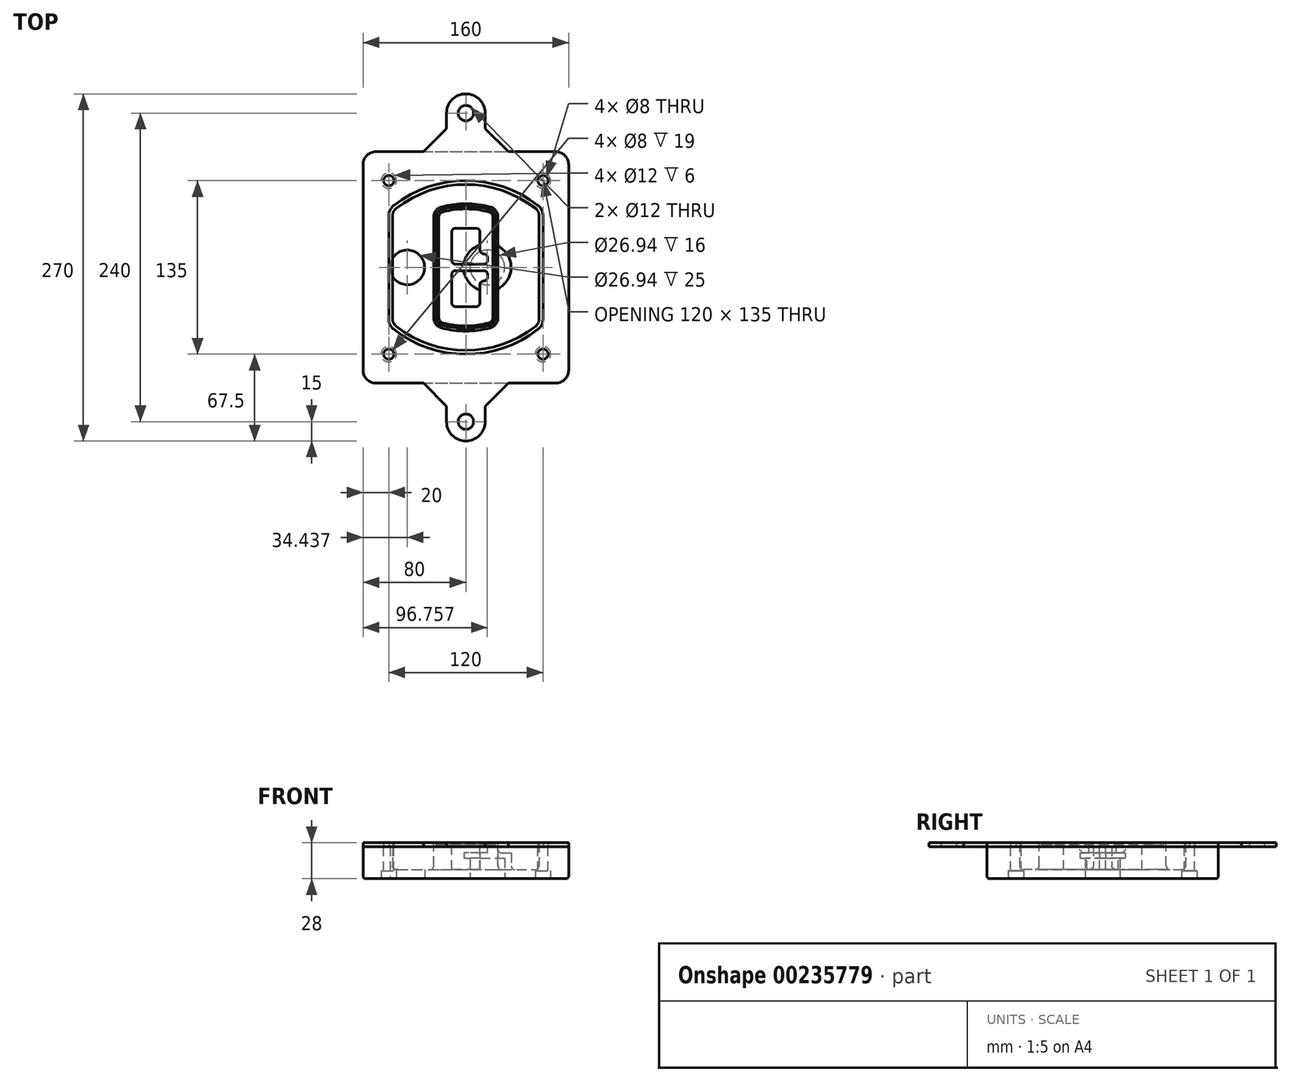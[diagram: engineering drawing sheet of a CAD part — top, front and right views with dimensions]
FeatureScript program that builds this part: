
annotation { "Feature Type Name" : "Feature", "Feature Type Description" : "" }
export const myFeature = defineFeature(function(context is Context, id is Id, definition is map)
    precondition{}
    {
        {
            var Q0;
            Q0=qCreatedBy(makeId("Top.planeOp"),FACE);
            var sketch = newSketch(context, id + "F0", { "sketchPlane" : qUnion([Q0])});
            skPoint(sketch, "E0.rect.middle", {"position": v(0, 0) * mm});
            skLineSegment(sketch, "E1.bottom", {"start": v(-70, -90) * mm, "end": v(70, -90) * mm});
            skLineSegment(sketch, "E1.top", {"start": v(-70, 90) * mm, "end": v(70, 90) * mm});
            skLineSegment(sketch, "E1.left", {"start": v(-80, -80) * mm, "end": v(-80, 80) * mm});
            skLineSegment(sketch, "E1.right", {"start": v(80, -80) * mm, "end": v(80, 80) * mm});
            skLineSegment(sketch, "E2", {"start": v(-80, 90) * mm, "end": v(80, -90) * mm, "construction": true});
            skLineSegment(sketch, "E3", {"start": v(80, 90) * mm, "end": v(-80, -90) * mm, "construction": true});
            skCircle(sketch, "E4", {"center": v(-60, 67.5) * mm, "radius": 4 * mm});
            skCircle(sketch, "E5", {"center": v(60, 67.5) * mm, "radius": 4 * mm});
            skCircle(sketch, "E6", {"center": v(60, -67.5) * mm, "radius": 4 * mm});
            skCircle(sketch, "E7", {"center": v(-60, -67.5) * mm, "radius": 4 * mm});
            skLineSegment(sketch, "E8", {"start": v(-60, 67.5) * mm, "end": v(60, 67.5) * mm, "construction": true});
            skLineSegment(sketch, "E9", {"start": v(60, 67.5) * mm, "end": v(60, -67.5) * mm, "construction": true});
            skLineSegment(sketch, "E10", {"start": v(60, -67.5) * mm, "end": v(-60, -67.5) * mm, "construction": true});
            skLineSegment(sketch, "E11", {"start": v(-60, -67.5) * mm, "end": v(-60, 67.5) * mm, "construction": true});
            skLineSegment(sketch, "E12", {"start": v(-60, 40.3) * mm, "end": v(-60, -40.3) * mm});
            skLineSegment(sketch, "E13", {"start": v(60, 40.3) * mm, "end": v(60, -40.3) * mm});
            skArc(sketch, "E14", {"start": v(56.15, 48.18) * mm, "mid": v(0, 67.5) * mm, "end": v(-56.15, 48.18) * mm});
            skArc(sketch, "E15", {"start": v(-56.15, -48.18) * mm, "mid": v(0, -67.5) * mm, "end": v(56.15, -48.18) * mm});
            skLineSegment(sketch, "E16", {"start": v(-60, 0) * mm, "end": v(60, 0) * mm, "construction": true});
            skPoint(sketch, "E17.visualSharp", {"position": v(-60, -45) * mm});
            skArc(sketch, "E17.filletArc", {"start": v(-60, -40.3) * mm, "mid": v(-58.99, -44.68) * mm, "end": v(-56.15, -48.18) * mm});
            skPoint(sketch, "E18.visualSharp", {"position": v(-60, 45) * mm});
            skArc(sketch, "E18.filletArc", {"start": v(-56.15, 48.18) * mm, "mid": v(-58.99, 44.68) * mm, "end": v(-60, 40.3) * mm});
            skPoint(sketch, "E19.visualSharp", {"position": v(60, 45) * mm});
            skArc(sketch, "E19.filletArc", {"start": v(60, 40.3) * mm, "mid": v(58.99, 44.68) * mm, "end": v(56.15, 48.18) * mm});
            skPoint(sketch, "E20.visualSharp", {"position": v(60, -45) * mm});
            skArc(sketch, "E20.filletArc", {"start": v(56.15, -48.18) * mm, "mid": v(58.99, -44.68) * mm, "end": v(60, -40.3) * mm});
            skPoint(sketch, "E21.visualSharp", {"position": v(-80, 90) * mm});
            skArc(sketch, "E21.filletArc", {"start": v(-70, 90) * mm, "mid": v(-77.07, 87.07) * mm, "end": v(-80, 80) * mm});
            skPoint(sketch, "E22.visualSharp", {"position": v(80, 90) * mm});
            skArc(sketch, "E22.filletArc", {"start": v(80, 80) * mm, "mid": v(77.07, 87.07) * mm, "end": v(70, 90) * mm});
            skPoint(sketch, "E23.visualSharp", {"position": v(80, -90) * mm});
            skArc(sketch, "E23.filletArc", {"start": v(70, -90) * mm, "mid": v(77.07, -87.07) * mm, "end": v(80, -80) * mm});
            skPoint(sketch, "E24.visualSharp", {"position": v(-80, -90) * mm});
            skArc(sketch, "E24.filletArc", {"start": v(-80, -80) * mm, "mid": v(-77.07, -87.07) * mm, "end": v(-70, -90) * mm});
            skArc(sketch, "E25.0", {"start": v(57, 40.3) * mm, "mid": v(56.3, 43.36) * mm, "end": v(54.3, 45.81) * mm});
            skLineSegment(sketch, "E25.1", {"start": v(57, 40.3) * mm, "end": v(57, -40.3) * mm});
            skArc(sketch, "E25.2", {"start": v(54.3, -45.81) * mm, "mid": v(56.3, -43.36) * mm, "end": v(57, -40.3) * mm});
            skArc(sketch, "E25.3", {"start": v(-54.3, -45.81) * mm, "mid": v(0, -64.5) * mm, "end": v(54.3, -45.81) * mm});
            skArc(sketch, "E25.4", {"start": v(-57, -40.3) * mm, "mid": v(-56.3, -43.36) * mm, "end": v(-54.3, -45.81) * mm});
            skArc(sketch, "E25.5", {"start": v(54.3, 45.81) * mm, "mid": v(0, 64.5) * mm, "end": v(-54.3, 45.81) * mm});
            skLineSegment(sketch, "E25.6", {"start": v(-57, 40.3) * mm, "end": v(-57, -40.3) * mm});
            skArc(sketch, "E25.7", {"start": v(-54.3, 45.81) * mm, "mid": v(-56.3, 43.36) * mm, "end": v(-57, 40.3) * mm});
            skArc(sketch, "E26.0", {"start": v(-58.62, 51.33) * mm, "mid": v(-62.58, 46.43) * mm, "end": v(-64, 40.3) * mm});
            skArc(sketch, "E26.1", {"start": v(58.62, 51.33) * mm, "mid": v(0, 71.5) * mm, "end": v(-58.62, 51.33) * mm});
            skArc(sketch, "E26.2", {"start": v(64, 40.3) * mm, "mid": v(62.58, 46.43) * mm, "end": v(58.62, 51.33) * mm});
            skLineSegment(sketch, "E26.3", {"start": v(64, 40.3) * mm, "end": v(64, -40.3) * mm});
            skArc(sketch, "E26.4", {"start": v(58.62, -51.33) * mm, "mid": v(62.58, -46.43) * mm, "end": v(64, -40.3) * mm});
            skLineSegment(sketch, "E26.5", {"start": v(-64, 40.3) * mm, "end": v(-64, -40.3) * mm});
            skArc(sketch, "E26.6", {"start": v(-58.62, -51.33) * mm, "mid": v(0, -71.5) * mm, "end": v(58.62, -51.33) * mm});
            skArc(sketch, "E26.7", {"start": v(-64, -40.3) * mm, "mid": v(-62.58, -46.43) * mm, "end": v(-58.62, -51.33) * mm});
            skSolve(sketch);
        }
        {
            var Q0;
            Q0=makeQuery(id+"F0.imprint","IMPRINT",FACE,{"disambiguationData":[TD([[makeQuery(id+"F0.imprint","IMPRINT",EDGE,{"derivedFrom":sQuery(id+"F0.wireOp",EDGE,"E1.bottom")}),1.0]])]});
            var Q1;
            Q1=makeQuery(id+"F0.imprint","IMPRINT",FACE,{"disambiguationData":[TD([[makeQuery(id+"F0.imprint","IMPRINT",EDGE,{"derivedFrom":sQuery(id+"F0.wireOp",EDGE,"E12")}),1.0]])]});
            var Q2;
            Q2=makeQuery(id+"F0.imprint","IMPRINT",FACE,{"disambiguationData":[TD([[makeQuery(id+"F0.imprint","IMPRINT",EDGE,{"derivedFrom":sQuery(id+"F0.wireOp",EDGE,"E25.0")}),1.0]])]});
            var Q3;
            Q3=makeQuery(id+"F0.imprint","IMPRINT",FACE,{"disambiguationData":[TD([[makeQuery(id+"F0.imprint","IMPRINT",EDGE,{"derivedFrom":sQuery(id+"F0.wireOp",EDGE,"E12")}),-1.0]])]});
            extrude(context, id + "F1", {"entities" : qUnion([Q0, Q1, Q2, Q3]), "oppositeDirection" : true, "depth" : 25 * mm});
        }
        {
            var Q0;
            Q0=makeQuery(id+"F0.imprint","IMPRINT",FACE,{"disambiguationData":[TD([[makeQuery(id+"F0.imprint","IMPRINT",EDGE,{"derivedFrom":sQuery(id+"F0.wireOp",EDGE,"E12")}),1.0]])]});
            extrude(context, id + "F2", {"entities" : qUnion([Q0]), "operationType" : NewBodyOperationType.ADD, "depth" : 3 * mm});
        }
        {
            var Q0;
            Q0=makeQuery(id+"F0.imprint","IMPRINT",FACE,{"disambiguationData":[TD([[makeQuery(id+"F0.imprint","IMPRINT",EDGE,{"derivedFrom":sQuery(id+"F0.wireOp",EDGE,"E25.0")}),1.0]])]});
            extrude(context, id + "F3", {"entities" : qUnion([Q0]), "operationType" : NewBodyOperationType.REMOVE, "oppositeDirection" : true, "depth" : 18 * mm});
        }
        {
            var Q0;
            Q0=makeQuery(id+"F2.opExtrude","CAP_FACE",FACE,{"disambiguationData":[OSD([sQuery(id+"F0.wireOp",EDGE,"E12"),sQuery(id+"F0.wireOp",EDGE,"E13"),sQuery(id+"F0.wireOp",EDGE,"E14"),sQuery(id+"F0.wireOp",EDGE,"E15"),sQuery(id+"F0.wireOp",EDGE,"E17.filletArc"),sQuery(id+"F0.wireOp",EDGE,"E18.filletArc"),sQuery(id+"F0.wireOp",EDGE,"E19.filletArc"),sQuery(id+"F0.wireOp",EDGE,"E20.filletArc"),sQuery(id+"F0.wireOp",EDGE,"E25.0"),sQuery(id+"F0.wireOp",EDGE,"E25.1"),sQuery(id+"F0.wireOp",EDGE,"E25.2"),sQuery(id+"F0.wireOp",EDGE,"E25.3"),sQuery(id+"F0.wireOp",EDGE,"E25.4"),sQuery(id+"F0.wireOp",EDGE,"E25.5"),sQuery(id+"F0.wireOp",EDGE,"E25.6"),sQuery(id+"F0.wireOp",EDGE,"E25.7")])],"isStart":false});
            var sketch = newSketch(context, id + "F4", { "sketchPlane" : qUnion([Q0])});
            skArc(sketch, "E27.0", {"start": v(-19.08, -46.97) * mm, "mid": v(0, -49.5) * mm, "end": v(19.08, -46.97) * mm});
            skArc(sketch, "E28.0", {"start": v(19.08, 46.97) * mm, "mid": v(0, 49.5) * mm, "end": v(-19.08, 46.97) * mm});
            skLineSegment(sketch, "E29", {"start": v(-25, 39.25) * mm, "end": v(-25, -39.25) * mm});
            skLineSegment(sketch, "E30", {"start": v(25, 39.25) * mm, "end": v(25, -39.25) * mm});
            skLineSegment(sketch, "E31", {"start": v(-25, 45.1) * mm, "end": v(25, 45.1) * mm, "construction": true});
            skLineSegment(sketch, "E32", {"start": v(-25, -45.1) * mm, "end": v(25, -45.1) * mm, "construction": true});
            skPoint(sketch, "E33.visualSharp", {"position": v(-25, 45.1) * mm});
            skArc(sketch, "E33.filletArc", {"start": v(-19.08, 46.97) * mm, "mid": v(-23.35, 44.11) * mm, "end": v(-25, 39.25) * mm});
            skPoint(sketch, "E34.visualSharp", {"position": v(25, 45.1) * mm});
            skArc(sketch, "E34.filletArc", {"start": v(25, 39.25) * mm, "mid": v(23.35, 44.11) * mm, "end": v(19.08, 46.97) * mm});
            skPoint(sketch, "E35.visualSharp", {"position": v(25, -45.1) * mm});
            skArc(sketch, "E35.filletArc", {"start": v(19.08, -46.97) * mm, "mid": v(23.35, -44.11) * mm, "end": v(25, -39.25) * mm});
            skPoint(sketch, "E36.visualSharp", {"position": v(-25, -45.1) * mm});
            skArc(sketch, "E36.filletArc", {"start": v(-25, -39.25) * mm, "mid": v(-23.35, -44.11) * mm, "end": v(-19.08, -46.97) * mm});
            skArc(sketch, "E37.0", {"start": v(54.3, 45.81) * mm, "mid": v(0, 64.5) * mm, "end": v(-54.3, 45.81) * mm});
            skArc(sketch, "E37.1", {"start": v(-54.3, 45.81) * mm, "mid": v(-56.3, 43.36) * mm, "end": v(-57, 40.3) * mm});
            skLineSegment(sketch, "E37.2", {"start": v(-57, 40.3) * mm, "end": v(-57, -40.3) * mm});
            skArc(sketch, "E37.3", {"start": v(-57, -40.3) * mm, "mid": v(-56.3, -43.36) * mm, "end": v(-54.3, -45.81) * mm});
            skArc(sketch, "E37.4", {"start": v(-54.3, -45.81) * mm, "mid": v(0, -64.5) * mm, "end": v(54.3, -45.81) * mm});
            skArc(sketch, "E37.5", {"start": v(54.3, -45.81) * mm, "mid": v(56.3, -43.36) * mm, "end": v(57, -40.3) * mm});
            skLineSegment(sketch, "E37.6", {"start": v(57, 40.3) * mm, "end": v(57, -40.3) * mm});
            skArc(sketch, "E37.7", {"start": v(57, 40.3) * mm, "mid": v(56.3, 43.36) * mm, "end": v(54.3, 45.81) * mm});
            skLineSegment(sketch, "E38.0", {"start": v(23, 39.25) * mm, "end": v(23, -39.25) * mm});
            skArc(sketch, "E38.1", {"start": v(18.56, -45.04) * mm, "mid": v(21.76, -42.9) * mm, "end": v(23, -39.25) * mm});
            skArc(sketch, "E38.2", {"start": v(-18.56, -45.04) * mm, "mid": v(0, -47.5) * mm, "end": v(18.56, -45.04) * mm});
            skArc(sketch, "E38.3", {"start": v(-23, -39.25) * mm, "mid": v(-21.76, -42.9) * mm, "end": v(-18.56, -45.04) * mm});
            skLineSegment(sketch, "E38.4", {"start": v(-23, 39.25) * mm, "end": v(-23, -39.25) * mm});
            skArc(sketch, "E38.5", {"start": v(23, 39.25) * mm, "mid": v(21.76, 42.9) * mm, "end": v(18.56, 45.04) * mm});
            skArc(sketch, "E38.6", {"start": v(-18.56, 45.04) * mm, "mid": v(-21.76, 42.9) * mm, "end": v(-23, 39.25) * mm});
            skArc(sketch, "E38.7", {"start": v(18.56, 45.04) * mm, "mid": v(0, 47.5) * mm, "end": v(-18.56, 45.04) * mm});
            skArc(sketch, "E39.0", {"start": v(21, 39.25) * mm, "mid": v(20.18, 41.68) * mm, "end": v(18.04, 43.1) * mm});
            skLineSegment(sketch, "E39.1", {"start": v(21, 39.25) * mm, "end": v(21, -39.25) * mm});
            skArc(sketch, "E39.2", {"start": v(18.04, -43.1) * mm, "mid": v(20.18, -41.68) * mm, "end": v(21, -39.25) * mm});
            skArc(sketch, "E39.3", {"start": v(-18.04, -43.1) * mm, "mid": v(0, -45.5) * mm, "end": v(18.04, -43.1) * mm});
            skArc(sketch, "E39.4", {"start": v(-21, -39.25) * mm, "mid": v(-20.18, -41.68) * mm, "end": v(-18.04, -43.1) * mm});
            skArc(sketch, "E39.5", {"start": v(18.04, 43.1) * mm, "mid": v(0, 45.5) * mm, "end": v(-18.04, 43.1) * mm});
            skLineSegment(sketch, "E39.6", {"start": v(-21, 39.25) * mm, "end": v(-21, -39.25) * mm});
            skArc(sketch, "E39.7", {"start": v(-18.04, 43.1) * mm, "mid": v(-20.18, 41.68) * mm, "end": v(-21, 39.25) * mm});
            skLineSegment(sketch, "E40", {"start": v(-25, 0) * mm, "end": v(25, 0) * mm, "construction": true});
            skLineSegment(sketch, "E41", {"start": v(-11, 5.5) * mm, "end": v(-11, 27.5) * mm});
            skLineSegment(sketch, "E42", {"start": v(-8, 30.5) * mm, "end": v(8, 30.5) * mm});
            skLineSegment(sketch, "E43", {"start": v(11, 27.5) * mm, "end": v(11, 13.5) * mm});
            skLineSegment(sketch, "E44", {"start": v(14, 10.5) * mm, "end": v(14, 10.5) * mm});
            skLineSegment(sketch, "E45", {"start": v(17, 7.5) * mm, "end": v(17, 5.5) * mm});
            skLineSegment(sketch, "E46", {"start": v(14, 2.5) * mm, "end": v(-8, 2.5) * mm});
            skPoint(sketch, "E47.visualSharp", {"position": v(-11, 30.5) * mm});
            skArc(sketch, "E47.filletArc", {"start": v(-8, 30.5) * mm, "mid": v(-10.12, 29.62) * mm, "end": v(-11, 27.5) * mm});
            skPoint(sketch, "E48.visualSharp", {"position": v(11, 30.5) * mm});
            skArc(sketch, "E48.filletArc", {"start": v(11, 27.5) * mm, "mid": v(10.12, 29.62) * mm, "end": v(8, 30.5) * mm});
            skPoint(sketch, "E49.visualSharp", {"position": v(11, 10.5) * mm});
            skArc(sketch, "E49.filletArc", {"start": v(11, 13.5) * mm, "mid": v(11.88, 11.38) * mm, "end": v(14, 10.5) * mm});
            skPoint(sketch, "E50.visualSharp", {"position": v(17, 10.5) * mm});
            skArc(sketch, "E50.filletArc", {"start": v(17, 7.5) * mm, "mid": v(16.12, 9.62) * mm, "end": v(14, 10.5) * mm});
            skPoint(sketch, "E51.visualSharp", {"position": v(17, 2.5) * mm});
            skArc(sketch, "E51.filletArc", {"start": v(14, 2.5) * mm, "mid": v(16.12, 3.38) * mm, "end": v(17, 5.5) * mm});
            skPoint(sketch, "E52.visualSharp", {"position": v(-11, 2.5) * mm});
            skArc(sketch, "E52.filletArc", {"start": v(-11, 5.5) * mm, "mid": v(-10.12, 3.38) * mm, "end": v(-8, 2.5) * mm});
            skLineSegment(sketch, "E53.0.MirrorCS", {"start": v(14, -2.5) * mm, "end": v(-8, -2.5) * mm});
            skArc(sketch, "E54.0.MirrorCS", {"start": v(-11, -5.5) * mm, "mid": v(-10.12, -3.38) * mm, "end": v(-8, -2.5) * mm});
            skLineSegment(sketch, "E55.0.MirrorCS", {"start": v(-11, -5.5) * mm, "end": v(-11, -27.5) * mm});
            skArc(sketch, "E56.0.MirrorCS", {"start": v(-8, -30.5) * mm, "mid": v(-10.12, -29.62) * mm, "end": v(-11, -27.5) * mm});
            skLineSegment(sketch, "E57.0.MirrorCS", {"start": v(-8, -30.5) * mm, "end": v(8, -30.5) * mm});
            skArc(sketch, "E58.0.MirrorCS", {"start": v(11, -27.5) * mm, "mid": v(10.12, -29.62) * mm, "end": v(8, -30.5) * mm});
            skLineSegment(sketch, "E59.0.MirrorCS", {"start": v(11, -27.5) * mm, "end": v(11, -13.5) * mm});
            skArc(sketch, "E60.0.MirrorCS", {"start": v(11, -13.5) * mm, "mid": v(11.88, -11.38) * mm, "end": v(14, -10.5) * mm});
            skArc(sketch, "E61.0.MirrorCS", {"start": v(17, -7.5) * mm, "mid": v(16.12, -9.62) * mm, "end": v(14, -10.5) * mm});
            skLineSegment(sketch, "E62.0.MirrorCS", {"start": v(17, -7.5) * mm, "end": v(17, -5.5) * mm});
            skArc(sketch, "E63.0.MirrorCS", {"start": v(14, -2.5) * mm, "mid": v(16.12, -3.38) * mm, "end": v(17, -5.5) * mm});
            skSolve(sketch);
        }
        {
            var Q0;
            Q0=makeQuery(id+"F4.imprint","IMPRINT",FACE,{"disambiguationData":[TD([[makeQuery(id+"F4.imprint","IMPRINT",EDGE,{"derivedFrom":sQuery(id+"F4.wireOp",EDGE,"E27.0")}),1.0]])]});
            var Q1;
            Q1=makeQuery(id+"F4.imprint","IMPRINT",FACE,{"disambiguationData":[TD([[makeQuery(id+"F4.imprint","IMPRINT",EDGE,{"derivedFrom":sQuery(id+"F4.wireOp",EDGE,"E38.0")}),-1.0]])]});
            var Q2;
            Q2=makeQuery(id+"F4.imprint","IMPRINT",FACE,{"disambiguationData":[TD([[makeQuery(id+"F4.imprint","IMPRINT",EDGE,{"derivedFrom":sQuery(id+"F4.wireOp",EDGE,"E39.0")}),1.0]])]});
            extrude(context, id + "F5", {"entities" : qUnion([Q0, Q1, Q2]), "operationType" : NewBodyOperationType.ADD, "endBound" : BoundingType.UP_TO_NEXT, "oppositeDirection" : true, "depth" : 25 * mm});
        }
        {
            var Q0;
            Q0=makeQuery(id+"F4.imprint","IMPRINT",FACE,{"disambiguationData":[TD([[makeQuery(id+"F4.imprint","IMPRINT",EDGE,{"derivedFrom":sQuery(id+"F4.wireOp",EDGE,"E38.0")}),-1.0]])]});
            extrude(context, id + "F6", {"entities" : qUnion([Q0]), "operationType" : NewBodyOperationType.REMOVE, "oppositeDirection" : true, "depth" : 2 * mm});
        }
        {
            var Q0;
            Q0=makeQuery(id+"F1.opExtrude","CAP_FACE",FACE,{"disambiguationData":[OSD([sQuery(id+"F0.wireOp",EDGE,"E1.bottom"),sQuery(id+"F0.wireOp",EDGE,"E1.top"),sQuery(id+"F0.wireOp",EDGE,"E1.left"),sQuery(id+"F0.wireOp",EDGE,"E1.right"),sQuery(id+"F0.wireOp",EDGE,"E4"),sQuery(id+"F0.wireOp",EDGE,"E5"),sQuery(id+"F0.wireOp",EDGE,"E6"),sQuery(id+"F0.wireOp",EDGE,"E7"),sQuery(id+"F0.wireOp",EDGE,"E21.filletArc"),sQuery(id+"F0.wireOp",EDGE,"E22.filletArc"),sQuery(id+"F0.wireOp",EDGE,"E23.filletArc"),sQuery(id+"F0.wireOp",EDGE,"E24.filletArc")])],"isStart":false});
            var sketch = newSketch(context, id + "F7", { "sketchPlane" : qUnion([Q0])});
            skCircle(sketch, "E64", {"center": v(16.76, 0) * mm, "radius": 13.47 * mm});
            skCircle(sketch, "E65", {"center": v(-45.56, 0) * mm, "radius": 13.47 * mm});
            skLineSegment(sketch, "E66", {"start": v(80, 0) * mm, "end": v(-80, 0) * mm});
            skCircle(sketch, "E67", {"center": v(16.76, 0) * mm, "radius": 18.47 * mm});
            skCircle(sketch, "E68", {"center": v(60, -67.5) * mm, "radius": 6 * mm});
            skCircle(sketch, "E69", {"center": v(-60, -67.5) * mm, "radius": 6 * mm});
            skCircle(sketch, "E70", {"center": v(-60, 67.5) * mm, "radius": 6 * mm});
            skCircle(sketch, "E71", {"center": v(60, 67.5) * mm, "radius": 6 * mm});
            skSolve(sketch);
        }
        {
            var Q0;
            {var subQ1=sQuery(id+"F7.wireOp",EDGE,"E66");var subQ4=sQuery(id+"F7.wireOp",EDGE,"E64");var subQ6=makeQuery(id+"F7.imprint","INTERSECT",VERTEX,{"disambiguationData":[OD(0.0)],"derivedFrom":[subQ4,subQ1]});Q0=makeQuery(id+"F7.imprint","IMPRINT",FACE,{"disambiguationData":[TD([[makeQuery(id+"F7.imprint","IMPRINT",EDGE,{"disambiguationData":[TD([[subQ6,-1.0]])],"derivedFrom":subQ4}),-1.0]])]});}
            var Q1;
            {var subQ0=sQuery(id+"F7.wireOp",EDGE,"E66");var subQ1=sQuery(id+"F7.wireOp",EDGE,"E64");var subQ3=makeQuery(id+"F7.imprint","INTERSECT",VERTEX,{"disambiguationData":[OD(0.0)],"derivedFrom":[subQ1,subQ0]});Q1=makeQuery(id+"F7.imprint","IMPRINT",FACE,{"disambiguationData":[TD([[makeQuery(id+"F7.imprint","IMPRINT",EDGE,{"disambiguationData":[TD([[subQ3,-1.0]])],"derivedFrom":subQ1}),1.0]])]});}
            var Q2;
            {var subQ0=sQuery(id+"F7.wireOp",EDGE,"E66");var subQ1=sQuery(id+"F7.wireOp",EDGE,"E64");var subQ3=makeQuery(id+"F7.imprint","INTERSECT",VERTEX,{"disambiguationData":[OD(0.0)],"derivedFrom":[subQ1,subQ0]});Q2=makeQuery(id+"F7.imprint","IMPRINT",FACE,{"disambiguationData":[TD([[makeQuery(id+"F7.imprint","IMPRINT",EDGE,{"disambiguationData":[TD([[subQ3,1.0]])],"derivedFrom":subQ1}),1.0]])]});}
            var Q3;
            {var subQ1=sQuery(id+"F7.wireOp",EDGE,"E66");var subQ4=sQuery(id+"F7.wireOp",EDGE,"E64");var subQ6=makeQuery(id+"F7.imprint","INTERSECT",VERTEX,{"disambiguationData":[OD(0.0)],"derivedFrom":[subQ4,subQ1]});Q3=makeQuery(id+"F7.imprint","IMPRINT",FACE,{"disambiguationData":[TD([[makeQuery(id+"F7.imprint","IMPRINT",EDGE,{"disambiguationData":[TD([[subQ6,1.0]])],"derivedFrom":subQ4}),-1.0]])]});}
            extrude(context, id + "F8", {"entities" : qUnion([Q0, Q1, Q2, Q3]), "operationType" : NewBodyOperationType.ADD, "oppositeDirection" : true, "depth" : 20 * mm});
        }
        {
            var Q0;
            {var subQ0=sQuery(id+"F7.wireOp",EDGE,"E66");var subQ1=sQuery(id+"F7.wireOp",EDGE,"E64");var subQ3=makeQuery(id+"F7.imprint","INTERSECT",VERTEX,{"disambiguationData":[OD(0.0)],"derivedFrom":[subQ1,subQ0]});Q0=makeQuery(id+"F7.imprint","IMPRINT",FACE,{"disambiguationData":[TD([[makeQuery(id+"F7.imprint","IMPRINT",EDGE,{"disambiguationData":[TD([[subQ3,-1.0]])],"derivedFrom":subQ1}),1.0]])]});}
            var Q1;
            {var subQ0=sQuery(id+"F7.wireOp",EDGE,"E66");var subQ1=sQuery(id+"F7.wireOp",EDGE,"E64");var subQ3=makeQuery(id+"F7.imprint","INTERSECT",VERTEX,{"disambiguationData":[OD(0.0)],"derivedFrom":[subQ1,subQ0]});Q1=makeQuery(id+"F7.imprint","IMPRINT",FACE,{"disambiguationData":[TD([[makeQuery(id+"F7.imprint","IMPRINT",EDGE,{"disambiguationData":[TD([[subQ3,1.0]])],"derivedFrom":subQ1}),1.0]])]});}
            extrude(context, id + "F9", {"entities" : qUnion([Q0, Q1]), "operationType" : NewBodyOperationType.REMOVE, "oppositeDirection" : true, "depth" : 16 * mm});
        }
        {
            var Q0;
            {var subQ0=sQuery(id+"F7.wireOp",EDGE,"E66");var subQ1=sQuery(id+"F7.wireOp",EDGE,"E65");var subQ3=makeQuery(id+"F7.imprint","INTERSECT",VERTEX,{"disambiguationData":[OD(0.0)],"derivedFrom":[subQ1,subQ0]});Q0=makeQuery(id+"F7.imprint","IMPRINT",FACE,{"disambiguationData":[TD([[makeQuery(id+"F7.imprint","IMPRINT",EDGE,{"disambiguationData":[TD([[subQ3,-1.0]])],"derivedFrom":subQ1}),1.0]])]});}
            var Q1;
            {var subQ0=sQuery(id+"F7.wireOp",EDGE,"E66");var subQ1=sQuery(id+"F7.wireOp",EDGE,"E65");var subQ3=makeQuery(id+"F7.imprint","INTERSECT",VERTEX,{"disambiguationData":[OD(0.0)],"derivedFrom":[subQ1,subQ0]});Q1=makeQuery(id+"F7.imprint","IMPRINT",FACE,{"disambiguationData":[TD([[makeQuery(id+"F7.imprint","IMPRINT",EDGE,{"disambiguationData":[TD([[subQ3,1.0]])],"derivedFrom":subQ1}),1.0]])]});}
            extrude(context, id + "F10", {"entities" : qUnion([Q0, Q1]), "operationType" : NewBodyOperationType.REMOVE, "oppositeDirection" : true, "depth" : 25 * mm});
        }
        {
            var Q0;
            Q0=makeQuery(id+"F7.imprint","IMPRINT",FACE,{"disambiguationData":[TD([[makeQuery(id+"F7.imprint","IMPRINT",EDGE,{"derivedFrom":sQuery(id+"F7.wireOp",EDGE,"E68")}),1.0]])]});
            var Q1;
            Q1=makeQuery(id+"F7.imprint","IMPRINT",FACE,{"disambiguationData":[TD([[makeQuery(id+"F7.imprint","IMPRINT",EDGE,{"derivedFrom":makeQuery(id+"F1.opExtrude","CAP_EDGE",EDGE,{"disambiguationData":[OSD([sQuery(id+"F0.wireOp",EDGE,"E5")])],"isStart":false})}),-1.0]])]});
            var Q2;
            Q2=makeQuery(id+"F7.imprint","IMPRINT",FACE,{"disambiguationData":[TD([[makeQuery(id+"F7.imprint","IMPRINT",EDGE,{"derivedFrom":sQuery(id+"F7.wireOp",EDGE,"E69")}),1.0]])]});
            var Q3;
            Q3=makeQuery(id+"F7.imprint","IMPRINT",FACE,{"disambiguationData":[TD([[makeQuery(id+"F7.imprint","IMPRINT",EDGE,{"derivedFrom":makeQuery(id+"F1.opExtrude","CAP_EDGE",EDGE,{"disambiguationData":[OSD([sQuery(id+"F0.wireOp",EDGE,"E4")])],"isStart":false})}),-1.0]])]});
            var Q4;
            Q4=makeQuery(id+"F7.imprint","IMPRINT",FACE,{"disambiguationData":[TD([[makeQuery(id+"F7.imprint","IMPRINT",EDGE,{"derivedFrom":sQuery(id+"F7.wireOp",EDGE,"E70")}),1.0]])]});
            var Q5;
            Q5=makeQuery(id+"F7.imprint","IMPRINT",FACE,{"disambiguationData":[TD([[makeQuery(id+"F7.imprint","IMPRINT",EDGE,{"derivedFrom":makeQuery(id+"F1.opExtrude","CAP_EDGE",EDGE,{"disambiguationData":[OSD([sQuery(id+"F0.wireOp",EDGE,"E7")])],"isStart":false})}),-1.0]])]});
            var Q6;
            Q6=makeQuery(id+"F7.imprint","IMPRINT",FACE,{"disambiguationData":[TD([[makeQuery(id+"F7.imprint","IMPRINT",EDGE,{"derivedFrom":sQuery(id+"F7.wireOp",EDGE,"E71")}),1.0]])]});
            var Q7;
            Q7=makeQuery(id+"F7.imprint","IMPRINT",FACE,{"disambiguationData":[TD([[makeQuery(id+"F7.imprint","IMPRINT",EDGE,{"derivedFrom":makeQuery(id+"F1.opExtrude","CAP_EDGE",EDGE,{"disambiguationData":[OSD([sQuery(id+"F0.wireOp",EDGE,"E6")])],"isStart":false})}),-1.0]])]});
            extrude(context, id + "F11", {"entities" : qUnion([Q0, Q1, Q2, Q3, Q4, Q5, Q6, Q7]), "operationType" : NewBodyOperationType.REMOVE, "oppositeDirection" : true, "depth" : 6 * mm});
        }
        {
            var Q0;
            Q0=makeQuery(id+"F9.boolean.opBoolean","COPY",FACE,{"derivedFrom":makeQuery(id+"F9.opExtrude","CAP_FACE",FACE,{"disambiguationData":[OSD([sQuery(id+"F7.wireOp",EDGE,"E64")])],"isStart":false})});
            var sketch = newSketch(context, id + "F12", { "sketchPlane" : qUnion([Q0])});
            skArc(sketch, "E72.0", {"start": v(11, 17.55) * mm, "mid": v(2.57, 11.82) * mm, "end": v(-1.54, 2.5) * mm});
            skArc(sketch, "E72.1", {"start": v(-1.54, -2.5) * mm, "mid": v(2.57, -11.82) * mm, "end": v(11, -17.55) * mm});
            skLineSegment(sketch, "E73", {"start": v(-1.54, -2.5) * mm, "end": v(14, -2.5) * mm});
            skLineSegment(sketch, "E74.0", {"start": v(14, 2.5) * mm, "end": v(-1.54, 2.5) * mm});
            skArc(sketch, "E74.1", {"start": v(14, 2.5) * mm, "mid": v(16.12, 3.38) * mm, "end": v(17, 5.5) * mm});
            skLineSegment(sketch, "E74.2", {"start": v(17, 7.5) * mm, "end": v(17, 5.5) * mm});
            skArc(sketch, "E74.3", {"start": v(17, 7.5) * mm, "mid": v(16.12, 9.62) * mm, "end": v(14, 10.5) * mm});
            skArc(sketch, "E74.4", {"start": v(11, 13.5) * mm, "mid": v(11.88, 11.38) * mm, "end": v(14, 10.5) * mm});
            skLineSegment(sketch, "E74.5", {"start": v(11, 17.55) * mm, "end": v(11, 13.5) * mm});
            skLineSegment(sketch, "E74.7", {"start": v(14, -2.5) * mm, "end": v(-1.54, -2.5) * mm});
            skArc(sketch, "E74.8", {"start": v(14, -2.5) * mm, "mid": v(16.12, -3.38) * mm, "end": v(17, -5.5) * mm});
            skLineSegment(sketch, "E74.9", {"start": v(17, -7.5) * mm, "end": v(17, -5.5) * mm});
            skArc(sketch, "E74.10", {"start": v(17, -7.5) * mm, "mid": v(16.12, -9.62) * mm, "end": v(14, -10.5) * mm});
            skArc(sketch, "E74.11", {"start": v(11, -13.5) * mm, "mid": v(11.88, -11.38) * mm, "end": v(14, -10.5) * mm});
            skLineSegment(sketch, "E74.12", {"start": v(11, -17.55) * mm, "end": v(11, -13.5) * mm});
            skPoint(sketch, "E75.orphan", {"position": v(11, -27.5) * mm});
            skPoint(sketch, "E76.orphan", {"position": v(-8, -2.5) * mm});
            skPoint(sketch, "E77.orphan", {"position": v(-8, 2.5) * mm});
            skPoint(sketch, "E78.orphan", {"position": v(11, 27.5) * mm});
            skSolve(sketch);
        }
        {
            var Q0;
            {var subQ7=sQuery(id+"F12.wireOp",EDGE,"E72.0");var subQ14=sQuery(id+"F12.wireOp",EDGE,"E72.1");var subQ16=sQuery(id+"F12.wireOp",EDGE,"E74.1");var subQ18=sQuery(id+"F12.wireOp",EDGE,"E74.8");Q0=qUnion([makeQuery(id+"F12.imprint","IMPRINT",FACE,{"disambiguationData":[TD([[makeQuery(id+"F12.imprint","IMPRINT",EDGE,{"derivedFrom":subQ7}),1.0]])]}),makeQuery(id+"F12.imprint","IMPRINT",FACE,{"disambiguationData":[TD([[makeQuery(id+"F12.imprint","IMPRINT",EDGE,{"derivedFrom":subQ14}),1.0]])]}),makeQuery(id+"F12.imprint","IMPRINT",FACE,{"disambiguationData":[TD([[makeQuery(id+"F12.imprint","IMPRINT",EDGE,{"derivedFrom":subQ16}),1.0]])]}),makeQuery(id+"F12.imprint","IMPRINT",FACE,{"disambiguationData":[TD([[makeQuery(id+"F12.imprint","IMPRINT",EDGE,{"derivedFrom":subQ18}),-1.0]])]})]);}
            var Q1;
            Q1=makeQuery(id+"F5.boolean.opBoolean","SPLIT",FACE,{"disambiguationData":[TD([makeQuery(id+"F5.opExtrude","SWEPT_FACE",FACE,{"disambiguationData":[OSD([sQuery(id+"F4.wireOp",EDGE,"E41")])]})])],"derivedFrom":makeQuery(id+"F3.boolean.opBoolean","COPY",FACE,{"derivedFrom":makeQuery(id+"F3.opExtrude","CAP_FACE",FACE,{"disambiguationData":[OSD([sQuery(id+"F0.wireOp",EDGE,"E25.0"),sQuery(id+"F0.wireOp",EDGE,"E25.1"),sQuery(id+"F0.wireOp",EDGE,"E25.2"),sQuery(id+"F0.wireOp",EDGE,"E25.3"),sQuery(id+"F0.wireOp",EDGE,"E25.4"),sQuery(id+"F0.wireOp",EDGE,"E25.5"),sQuery(id+"F0.wireOp",EDGE,"E25.6"),sQuery(id+"F0.wireOp",EDGE,"E25.7")])],"isStart":false})})});
            extrude(context, id + "F13", {"entities" : qUnion([Q0]), "operationType" : NewBodyOperationType.REMOVE, "endBound" : BoundingType.UP_TO_SURFACE, "endBoundEntityFace" : qUnion([Q1]), "depth" : 25 * mm});
        }
        {
            var Q0;
            Q0=makeQuery(id+"F3.boolean.opBoolean","COPY",EDGE,{"derivedFrom":makeQuery(id+"F3.opExtrude","CAP_EDGE",EDGE,{"disambiguationData":[OSD([sQuery(id+"F0.wireOp",EDGE,"E25.6")])],"isStart":false})});
            var Q1;
            Q1=makeQuery(id+"F8.boolean.opBoolean","INTERSECT",EDGE,{"derivedFrom":[makeQuery(id+"F5.opExtrude","SWEPT_FACE",FACE,{"disambiguationData":[OSD([sQuery(id+"F4.wireOp",EDGE,"E30")])]}),makeQuery(id+"F8.opExtrude","CAP_FACE",FACE,{"disambiguationData":[OSD([sQuery(id+"F7.wireOp",EDGE,"E67")])],"isStart":false})]});
            var Q2;
            Q2=makeQuery(id+"F8.boolean.opBoolean","INTERSECT",EDGE,{"disambiguationData":[OD(1.0)],"derivedFrom":[makeQuery(id+"F5.opExtrude","SWEPT_FACE",FACE,{"disambiguationData":[OSD([sQuery(id+"F4.wireOp",EDGE,"E30")])]}),makeQuery(id+"F8.opExtrude","SWEPT_FACE",FACE,{"disambiguationData":[OSD([sQuery(id+"F7.wireOp",EDGE,"E67")])]})]});
            var Q3;
            {var subQ0=sQuery(id+"F4.wireOp",EDGE,"E30");Q3=makeQuery(id+"F8.boolean.opBoolean","SPLIT",EDGE,{"disambiguationData":[TD([makeQuery(id+"F5.opExtrude","SWEPT_FACE",FACE,{"disambiguationData":[OSD([sQuery(id+"F4.wireOp",EDGE,"E35.filletArc")])]})])],"derivedFrom":makeQuery(id+"F5.opExtrude","CAP_EDGE",EDGE,{"disambiguationData":[OSD([subQ0])],"isStart":false})});}
            var Q4;
            {var subQ0=sQuery(id+"F0.wireOp",EDGE,"E25.7");var subQ1=sQuery(id+"F0.wireOp",EDGE,"E25.1");var subQ2=sQuery(id+"F0.wireOp",EDGE,"E25.6");var subQ3=sQuery(id+"F0.wireOp",EDGE,"E25.5");var subQ4=sQuery(id+"F0.wireOp",EDGE,"E25.4");var subQ5=sQuery(id+"F0.wireOp",EDGE,"E25.0");var subQ6=sQuery(id+"F0.wireOp",EDGE,"E25.2");var subQ7=sQuery(id+"F0.wireOp",EDGE,"E25.3");Q4=makeQuery(id+"F8.boolean.opBoolean","INTERSECT",EDGE,{"derivedFrom":[makeQuery(id+"F5.boolean.opBoolean","SPLIT",FACE,{"disambiguationData":[TD([makeQuery(id+"F2.opExtrude","SWEPT_FACE",FACE,{"disambiguationData":[OSD([subQ5])]})])],"derivedFrom":makeQuery(id+"F3.boolean.opBoolean","COPY",FACE,{"derivedFrom":makeQuery(id+"F3.opExtrude","CAP_FACE",FACE,{"disambiguationData":[OSD([subQ5,subQ1,subQ6,subQ7,subQ4,subQ3,subQ2,subQ0])],"isStart":false})})}),makeQuery(id+"F8.opExtrude","SWEPT_FACE",FACE,{"disambiguationData":[OSD([sQuery(id+"F7.wireOp",EDGE,"E67")])]})]});}
            var Q5;
            Q5=makeQuery(id+"F8.boolean.opBoolean","INTERSECT",EDGE,{"disambiguationData":[OD(0.0)],"derivedFrom":[makeQuery(id+"F5.opExtrude","SWEPT_FACE",FACE,{"disambiguationData":[OSD([sQuery(id+"F4.wireOp",EDGE,"E30")])]}),makeQuery(id+"F8.opExtrude","SWEPT_FACE",FACE,{"disambiguationData":[OSD([sQuery(id+"F7.wireOp",EDGE,"E67")])]})]});
            fillet(context, id + "F14", {"entities" : qUnion([Q0, Q1, Q2, Q3, Q4, Q5]), "radius" : 3 * mm, "tangentPropagation" : true, "allowEdgeOverflow" : false});
        }
        {
            var Q0;
            Q0=makeQuery(id+"F1.opExtrude","CAP_EDGE",EDGE,{"disambiguationData":[OSD([sQuery(id+"F0.wireOp",EDGE,"E1.bottom")])],"isStart":false});
            fillet(context, id + "F15", {"entities" : qUnion([Q0]), "radius" : 2 * mm, "tangentPropagation" : true, "allowEdgeOverflow" : false});
        }
        {
            var Q0;
            {var subQ0=sQuery(id+"F0.wireOp",EDGE,"E22.filletArc");var subQ1=sQuery(id+"F0.wireOp",EDGE,"E7");var subQ2=sQuery(id+"F0.wireOp",EDGE,"E6");var subQ3=sQuery(id+"F0.wireOp",EDGE,"E5");var subQ4=sQuery(id+"F0.wireOp",EDGE,"E4");var subQ5=sQuery(id+"F0.wireOp",EDGE,"E1.bottom");var subQ6=sQuery(id+"F0.wireOp",EDGE,"E21.filletArc");var subQ7=sQuery(id+"F0.wireOp",EDGE,"E1.top");var subQ8=sQuery(id+"F0.wireOp",EDGE,"E1.left");var subQ9=sQuery(id+"F0.wireOp",EDGE,"E1.right");var subQ10=sQuery(id+"F0.wireOp",EDGE,"E23.filletArc");var subQ11=sQuery(id+"F0.wireOp",EDGE,"E24.filletArc");Q0=makeQuery(id+"F2.boolean.opBoolean","SPLIT",FACE,{"disambiguationData":[TD([makeQuery(id+"F1.opExtrude","SWEPT_FACE",FACE,{"disambiguationData":[OSD([subQ5])]})])],"derivedFrom":makeQuery(id+"F1.opExtrude","CAP_FACE",FACE,{"disambiguationData":[OSD([subQ5,subQ7,subQ8,subQ9,subQ4,subQ3,subQ2,subQ1,subQ6,subQ0,subQ10,subQ11])],"isStart":true})});}
            var sketch = newSketch(context, id + "F16", { "sketchPlane" : qUnion([Q0])});
            skLineSegment(sketch, "E79", {"start": v(-33, 90) * mm, "end": v(-15, 108) * mm});
            skLineSegment(sketch, "E80", {"start": v(-15, 108) * mm, "end": v(-15, 120) * mm});
            skLineSegment(sketch, "E81", {"start": v(33, 90) * mm, "end": v(15, 108) * mm});
            skLineSegment(sketch, "E82", {"start": v(15, 108) * mm, "end": v(15, 120) * mm});
            skArc(sketch, "E83", {"start": v(15, 120) * mm, "mid": v(0, 135) * mm, "end": v(-15, 120) * mm});
            skCircle(sketch, "E84", {"center": v(0, 120) * mm, "radius": 6 * mm});
            skLineSegment(sketch, "E85", {"start": v(0, 90) * mm, "end": v(0, 120) * mm, "construction": true});
            skLineSegment(sketch, "E86", {"start": v(-80, 0) * mm, "end": v(80, 0) * mm, "construction": true});
            skLineSegment(sketch, "E87.MirrorCS", {"start": v(-33, -90) * mm, "end": v(-15, -108) * mm});
            skLineSegment(sketch, "E88.MirrorCS", {"start": v(-15, -108) * mm, "end": v(-15, -120) * mm});
            skLineSegment(sketch, "E89.MirrorCS", {"start": v(33, -90) * mm, "end": v(15, -108) * mm});
            skLineSegment(sketch, "E90.MirrorCS", {"start": v(15, -108) * mm, "end": v(15, -120) * mm});
            skArc(sketch, "E91.MirrorCS", {"start": v(15, -120) * mm, "mid": v(0, -135) * mm, "end": v(-15, -120) * mm});
            skCircle(sketch, "E92.MirrorC", {"center": v(0, -120) * mm, "radius": 6 * mm});
            skLineSegment(sketch, "E93.MirrorCS", {"start": v(0, -90) * mm, "end": v(0, -120) * mm, "construction": true});
            skSolve(sketch);
        }
        {
            var Q0;
            {var subQ1=sQuery(id+"F16.wireOp",EDGE,"E79");Q0=makeQuery(id+"F16.imprint","IMPRINT",FACE,{"disambiguationData":[TD([[makeQuery(id+"F16.imprint","IMPRINT",EDGE,{"derivedFrom":subQ1}),-1.0]])]});}
            var Q1;
            {var subQ1=sQuery(id+"F16.wireOp",EDGE,"E87.MirrorCS");Q1=makeQuery(id+"F16.imprint","IMPRINT",FACE,{"disambiguationData":[TD([[makeQuery(id+"F16.imprint","IMPRINT",EDGE,{"derivedFrom":subQ1}),1.0]])]});}
            var Q2;
            Q2=makeQuery(id+"F16.imprint","IMPRINT",FACE,{"disambiguationData":[TD([[makeQuery(id+"F16.imprint","IMPRINT",EDGE,{"derivedFrom":makeQuery(id+"F1.opExtrude","CAP_EDGE",EDGE,{"disambiguationData":[OSD([sQuery(id+"F0.wireOp",EDGE,"E1.left")])],"isStart":true})}),-1.0]])]});
            var Q3;
            Q3=makeQuery(id+"F2.opExtrude","CAP_FACE",FACE,{"disambiguationData":[OSD([sQuery(id+"F0.wireOp",EDGE,"E12"),sQuery(id+"F0.wireOp",EDGE,"E13"),sQuery(id+"F0.wireOp",EDGE,"E14"),sQuery(id+"F0.wireOp",EDGE,"E15"),sQuery(id+"F0.wireOp",EDGE,"E17.filletArc"),sQuery(id+"F0.wireOp",EDGE,"E18.filletArc"),sQuery(id+"F0.wireOp",EDGE,"E19.filletArc"),sQuery(id+"F0.wireOp",EDGE,"E20.filletArc"),sQuery(id+"F0.wireOp",EDGE,"E25.0"),sQuery(id+"F0.wireOp",EDGE,"E25.1"),sQuery(id+"F0.wireOp",EDGE,"E25.2"),sQuery(id+"F0.wireOp",EDGE,"E25.3"),sQuery(id+"F0.wireOp",EDGE,"E25.4"),sQuery(id+"F0.wireOp",EDGE,"E25.5"),sQuery(id+"F0.wireOp",EDGE,"E25.6"),sQuery(id+"F0.wireOp",EDGE,"E25.7")])],"isStart":false});
            extrude(context, id + "F17", {"entities" : qUnion([Q0, Q1, Q2]), "endBound" : BoundingType.UP_TO_SURFACE, "endBoundEntityFace" : qUnion([Q3]), "depth" : 25 * mm});
        }
    });
